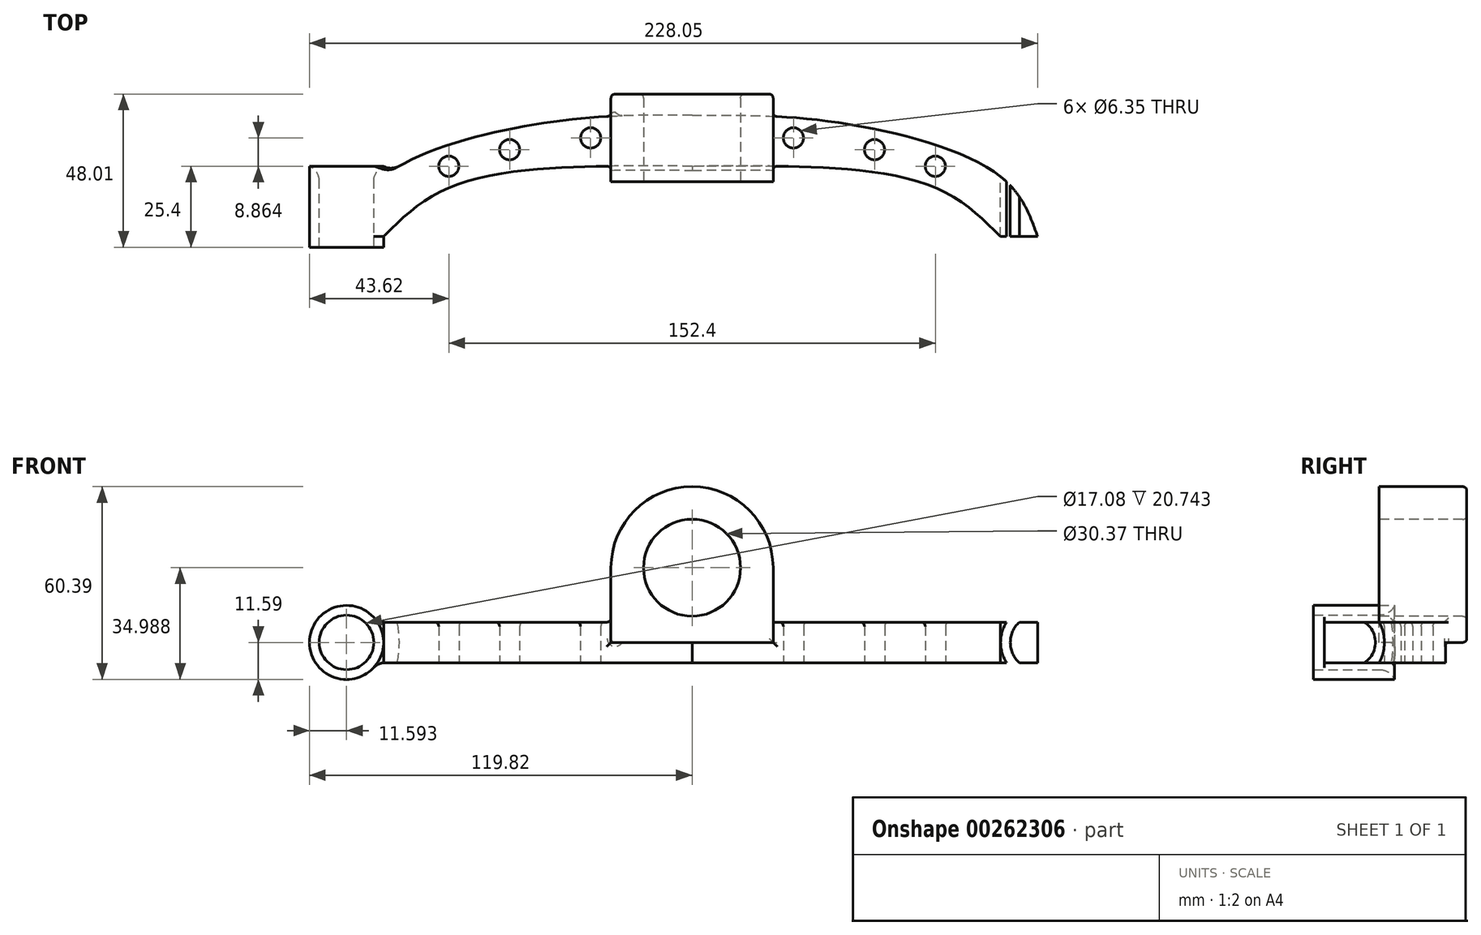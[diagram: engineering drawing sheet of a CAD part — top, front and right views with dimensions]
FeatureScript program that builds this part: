
annotation { "Feature Type Name" : "Feature", "Feature Type Description" : "" }
export const myFeature = defineFeature(function(context is Context, id is Id, definition is map)
    precondition{}
    {
        {
            var Q0;
            Q0=qCreatedBy(makeId("Top.planeOp"),FACE);
            var sketch = newSketch(context, id + "F0", { "sketchPlane" : qUnion([Q0])});
            skFitSpline(sketch, "E0", {"points": [v(0, 15.99) * mm, v(-43.29, 14) * mm, v(-96.35, -3.02) * mm, v(-108.23, -22.03) * mm], "startDerivative": vector(-114.23, 0) * mm, "endDerivative": vector(-28.32, -80.2) * mm});
            skLineSegment(sketch, "E1", {"start": v(0, 49.85) * mm, "end": v(0, -44) * mm, "construction": true});
            skFitSpline(sketch, "E2.MirrorCS", {"points": [v(0, 15.99) * mm, v(43.29, 14) * mm, v(96.35, -3.02) * mm, v(108.23, -22.03) * mm], "startDerivative": vector(114.23, 0) * mm, "endDerivative": vector(28.32, -80.2) * mm});
            skFitSpline(sketch, "E3", {"points": [v(0, 0) * mm, v(-27.26, 0) * mm, v(-73.98, -5.82) * mm, v(-96.64, -22.03) * mm], "startDerivative": vector(-81.32, 0.87) * mm, "endDerivative": vector(-62.2, -62.12) * mm});
            skFitSpline(sketch, "E4.MirrorCS", {"points": [v(0, 0) * mm, v(27.26, 0) * mm, v(73.98, -5.82) * mm, v(96.64, -22.03) * mm], "startDerivative": vector(81.32, 0.87) * mm, "endDerivative": vector(62.2, -62.12) * mm});
            skLineSegment(sketch, "E5", {"start": v(-96.64, -22.03) * mm, "end": v(-108.23, -22.03) * mm});
            skLineSegment(sketch, "E6", {"start": v(96.64, -22.03) * mm, "end": v(108.23, -22.03) * mm});
            skCircle(sketch, "E7", {"center": v(-76.2, 0) * mm, "radius": 3.18 * mm});
            skCircle(sketch, "E8", {"center": v(-57.15, 5.18) * mm, "radius": 3.18 * mm});
            skCircle(sketch, "E9", {"center": v(-31.75, 8.86) * mm, "radius": 3.18 * mm});
            skFitSpline(sketch, "E10.0", {"points": [v(0, 9.64) * mm, v(-2.4, 9.64) * mm, v(-7.16, 9.65) * mm, v(-14.32, 9.63) * mm, v(-21.64, 9.48) * mm, v(-27.97, 9.16) * mm, v(-33.23, 8.75) * mm, v(-37.3, 8.35) * mm, v(-41.49, 7.86) * mm, v(-45.84, 7.24) * mm, v(-50.31, 6.51) * mm, v(-56.36, 5.39) * mm, v(-63.97, 3.7) * mm, v(-71.31, 1.65) * mm, v(-76.8, -0.18) * mm, v(-80.7, -1.65) * mm, v(-84.28, -3.2) * mm, v(-86.97, -4.55) * mm, v(-88.92, -5.65) * mm, v(-90.27, -6.48) * mm, v(-91.3, -7.18) * mm, v(-92.06, -7.73) * mm, v(-92.77, -8.28) * mm, v(-93.6, -8.97) * mm, v(-94.8, -10.09) * mm, v(-96.1, -11.52) * mm, v(-97.43, -13.3) * mm, v(-98.57, -15.2) * mm, v(-99.58, -17.21) * mm, v(-100.8, -20.1) * mm, v(-101.65, -22.47) * mm, v(-102.24, -24.14) * mm], "construction": true});
            skCircle(sketch, "E11.MirrorC", {"center": v(31.75, 8.86) * mm, "radius": 3.18 * mm});
            skCircle(sketch, "E12.MirrorC", {"center": v(57.15, 5.18) * mm, "radius": 3.18 * mm});
            skCircle(sketch, "E13.MirrorC", {"center": v(76.2, 0) * mm, "radius": 3.18 * mm});
            skSolve(sketch);
        }
        {
            var Q0;
            Q0=makeQuery(id+"F0.imprint","IMPRINT",FACE,{"disambiguationData":[TD([[makeQuery(id+"F0.imprint","IMPRINT",EDGE,{"derivedFrom":sQuery(id+"F0.wireOp",EDGE,"E0")}),1.0]])]});
            extrude(context, id + "F1", {"entities" : qUnion([Q0]), "endBound" : BoundingType.SYMMETRIC, "depth" : 12.7 * mm});
        }
        {
            var Q0;
            Q0=makeQuery(id+"F1.opExtrude","CAP_EDGE",EDGE,{"disambiguationData":[OSD([sQuery(id+"F0.wireOp",EDGE,"E7")])],"isStart":false});
            var Q1;
            Q1=makeQuery(id+"F1.opExtrude","CAP_EDGE",EDGE,{"disambiguationData":[OSD([sQuery(id+"F0.wireOp",EDGE,"E8")])],"isStart":false});
            var Q2;
            Q2=makeQuery(id+"F1.opExtrude","CAP_EDGE",EDGE,{"disambiguationData":[OSD([sQuery(id+"F0.wireOp",EDGE,"E9")])],"isStart":false});
            var Q3;
            Q3=makeQuery(id+"F1.opExtrude","CAP_EDGE",EDGE,{"disambiguationData":[OSD([sQuery(id+"F0.wireOp",EDGE,"E11.MirrorC")])],"isStart":false});
            var Q4;
            Q4=makeQuery(id+"F1.opExtrude","CAP_EDGE",EDGE,{"disambiguationData":[OSD([sQuery(id+"F0.wireOp",EDGE,"E12.MirrorC")])],"isStart":false});
            var Q5;
            Q5=makeQuery(id+"F1.opExtrude","CAP_EDGE",EDGE,{"disambiguationData":[OSD([sQuery(id+"F0.wireOp",EDGE,"E13.MirrorC")])],"isStart":false});
            fillet(context, id + "F2", {"entities" : qUnion([Q0, Q1, Q2, Q3, Q4, Q5]), "radius" : 1.27 * mm, "tangentPropagation" : true, "allowEdgeOverflow" : false});
        }
        {
            var Q0;
            Q0=qCreatedBy(makeId("Front.planeOp"),FACE);
            var sketch = newSketch(context, id + "F3", { "sketchPlane" : qUnion([Q0])});
            skPoint(sketch, "E14.0", {"position": v(-96.64, 0) * mm});
            skPoint(sketch, "E15.0", {"position": v(-108.23, 0) * mm});
            skCircle(sketch, "E16", {"center": v(-108.23, 0) * mm, "radius": 11.6 * mm});
            skCircle(sketch, "E17", {"center": v(-108.23, 0) * mm, "radius": 8.54 * mm});
            skLineSegment(sketch, "E18", {"start": v(0, 0) * mm, "end": v(0, 47.64) * mm, "construction": true});
            skCircle(sketch, "E19.MirrorC", {"center": v(108.23, 0) * mm, "radius": 11.6 * mm});
            skCircle(sketch, "E20.MirrorC", {"center": v(108.23, 0) * mm, "radius": 8.54 * mm});
            skSolve(sketch);
        }
        {
            var Q0;
            Q0=makeQuery(id+"F3.imprint","IMPRINT",FACE,{"disambiguationData":[TD([[makeQuery(id+"F3.imprint","IMPRINT",EDGE,{"derivedFrom":sQuery(id+"F3.wireOp",EDGE,"E16")}),1.0]])]});
            var Q1;
            Q1=makeQuery(id+"F3.imprint","IMPRINT",FACE,{"disambiguationData":[TD([[makeQuery(id+"F3.imprint","IMPRINT",EDGE,{"derivedFrom":sQuery(id+"F3.wireOp",EDGE,"E19.MirrorC")}),-1.0]])]});
            extrude(context, id + "F4", {"entities" : qUnion([Q0, Q1]), "operationType" : NewBodyOperationType.ADD, "depth" : 25.4 * mm});
        }
        {
            var Q0;
            Q0=makeQuery(id+"F3.imprint","IMPRINT",FACE,{"disambiguationData":[TD([[makeQuery(id+"F3.imprint","IMPRINT",EDGE,{"derivedFrom":sQuery(id+"F3.wireOp",EDGE,"E17")}),1.0]])]});
            var Q1;
            Q1=makeQuery(id+"F3.imprint","IMPRINT",FACE,{"disambiguationData":[TD([[makeQuery(id+"F3.imprint","IMPRINT",EDGE,{"derivedFrom":sQuery(id+"F3.wireOp",EDGE,"E20.MirrorC")}),-1.0]])]});
            extrude(context, id + "F5", {"entities" : qUnion([Q0, Q1]), "operationType" : NewBodyOperationType.REMOVE, "endBound" : BoundingType.THROUGH_ALL, "depth" : 25.4 * mm});
        }
        {
            var Q0;
            Q0=makeQuery(id+"F4.opExtrude","CAP_EDGE",EDGE,{"disambiguationData":[OSD([sQuery(id+"F3.wireOp",EDGE,"E17")])],"isStart":true});
            var Q1;
            Q1=makeQuery(id+"F4.boolean.opBoolean","INTERSECT",EDGE,{"derivedFrom":[makeQuery(id+"F1.opExtrude","CAP_FACE",FACE,{"disambiguationData":[OSD([sQuery(id+"F0.wireOp",EDGE,"E0"),sQuery(id+"F0.wireOp",EDGE,"E2.MirrorCS"),sQuery(id+"F0.wireOp",EDGE,"E3"),sQuery(id+"F0.wireOp",EDGE,"E4.MirrorCS"),sQuery(id+"F0.wireOp",EDGE,"E5"),sQuery(id+"F0.wireOp",EDGE,"E6"),sQuery(id+"F0.wireOp",EDGE,"E7"),sQuery(id+"F0.wireOp",EDGE,"E8"),sQuery(id+"F0.wireOp",EDGE,"E9"),sQuery(id+"F0.wireOp",EDGE,"E11.MirrorC"),sQuery(id+"F0.wireOp",EDGE,"E12.MirrorC"),sQuery(id+"F0.wireOp",EDGE,"E13.MirrorC")])],"isStart":false}),makeQuery(id+"F4.opExtrude","SWEPT_FACE",FACE,{"disambiguationData":[OSD([sQuery(id+"F3.wireOp",EDGE,"E16")])]})]});
            var Q2;
            Q2=makeQuery(id+"F4.boolean.opBoolean","INTERSECT",EDGE,{"derivedFrom":[makeQuery(id+"F1.opExtrude","SWEPT_FACE",FACE,{"disambiguationData":[OSD([sQuery(id+"F0.wireOp",EDGE,"E0")])]}),makeQuery(id+"F4.opExtrude","SWEPT_FACE",FACE,{"disambiguationData":[OSD([sQuery(id+"F3.wireOp",EDGE,"E16")])]})]});
            var Q3;
            Q3=makeQuery(id+"F4.boolean.opBoolean","INTERSECT",EDGE,{"derivedFrom":[makeQuery(id+"F1.opExtrude","CAP_FACE",FACE,{"disambiguationData":[OSD([sQuery(id+"F0.wireOp",EDGE,"E0"),sQuery(id+"F0.wireOp",EDGE,"E2.MirrorCS"),sQuery(id+"F0.wireOp",EDGE,"E3"),sQuery(id+"F0.wireOp",EDGE,"E4.MirrorCS"),sQuery(id+"F0.wireOp",EDGE,"E5"),sQuery(id+"F0.wireOp",EDGE,"E6"),sQuery(id+"F0.wireOp",EDGE,"E7"),sQuery(id+"F0.wireOp",EDGE,"E8"),sQuery(id+"F0.wireOp",EDGE,"E9"),sQuery(id+"F0.wireOp",EDGE,"E11.MirrorC"),sQuery(id+"F0.wireOp",EDGE,"E12.MirrorC"),sQuery(id+"F0.wireOp",EDGE,"E13.MirrorC")])],"isStart":true}),makeQuery(id+"F4.opExtrude","SWEPT_FACE",FACE,{"disambiguationData":[OSD([sQuery(id+"F3.wireOp",EDGE,"E16")])]})]});
            var Q4;
            Q4=makeQuery(id+"F4.opExtrude","CAP_EDGE",EDGE,{"disambiguationData":[OSD([sQuery(id+"F3.wireOp",EDGE,"E20.MirrorC")])],"isStart":true});
            var Q5;
            Q5=makeQuery(id+"F4.boolean.opBoolean","INTERSECT",EDGE,{"derivedFrom":[makeQuery(id+"F1.opExtrude","CAP_FACE",FACE,{"disambiguationData":[OSD([sQuery(id+"F0.wireOp",EDGE,"E0"),sQuery(id+"F0.wireOp",EDGE,"E2.MirrorCS"),sQuery(id+"F0.wireOp",EDGE,"E3"),sQuery(id+"F0.wireOp",EDGE,"E4.MirrorCS"),sQuery(id+"F0.wireOp",EDGE,"E5"),sQuery(id+"F0.wireOp",EDGE,"E6"),sQuery(id+"F0.wireOp",EDGE,"E7"),sQuery(id+"F0.wireOp",EDGE,"E8"),sQuery(id+"F0.wireOp",EDGE,"E9"),sQuery(id+"F0.wireOp",EDGE,"E11.MirrorC"),sQuery(id+"F0.wireOp",EDGE,"E12.MirrorC"),sQuery(id+"F0.wireOp",EDGE,"E13.MirrorC")])],"isStart":false}),makeQuery(id+"F4.opExtrude","SWEPT_FACE",FACE,{"disambiguationData":[OSD([sQuery(id+"F3.wireOp",EDGE,"E19.MirrorC")])]})]});
            var Q6;
            Q6=makeQuery(id+"F4.boolean.opBoolean","INTERSECT",EDGE,{"derivedFrom":[makeQuery(id+"F1.opExtrude","SWEPT_FACE",FACE,{"disambiguationData":[OSD([sQuery(id+"F0.wireOp",EDGE,"E2.MirrorCS")])]}),makeQuery(id+"F4.opExtrude","SWEPT_FACE",FACE,{"disambiguationData":[OSD([sQuery(id+"F3.wireOp",EDGE,"E19.MirrorC")])]})]});
            var Q7;
            Q7=makeQuery(id+"F4.boolean.opBoolean","INTERSECT",EDGE,{"derivedFrom":[makeQuery(id+"F1.opExtrude","CAP_FACE",FACE,{"disambiguationData":[OSD([sQuery(id+"F0.wireOp",EDGE,"E0"),sQuery(id+"F0.wireOp",EDGE,"E2.MirrorCS"),sQuery(id+"F0.wireOp",EDGE,"E3"),sQuery(id+"F0.wireOp",EDGE,"E4.MirrorCS"),sQuery(id+"F0.wireOp",EDGE,"E5"),sQuery(id+"F0.wireOp",EDGE,"E6"),sQuery(id+"F0.wireOp",EDGE,"E7"),sQuery(id+"F0.wireOp",EDGE,"E8"),sQuery(id+"F0.wireOp",EDGE,"E9"),sQuery(id+"F0.wireOp",EDGE,"E11.MirrorC"),sQuery(id+"F0.wireOp",EDGE,"E12.MirrorC"),sQuery(id+"F0.wireOp",EDGE,"E13.MirrorC")])],"isStart":true}),makeQuery(id+"F4.opExtrude","SWEPT_FACE",FACE,{"disambiguationData":[OSD([sQuery(id+"F3.wireOp",EDGE,"E19.MirrorC")])]})]});
            fillet(context, id + "F6", {"entities" : qUnion([Q0, Q1, Q2, Q3, Q4, Q5, Q6, Q7]), "radius" : 5.08 * mm, "tangentPropagation" : true, "allowEdgeOverflow" : false});
        }
        {
            var Q0;
            Q0=qCreatedBy(makeId("Front.planeOp"),FACE);
            var sketch = newSketch(context, id + "F7", { "sketchPlane" : qUnion([Q0])});
            skLineSegment(sketch, "E21", {"start": v(0, -20.34) * mm, "end": v(0, 23.4) * mm, "construction": true});
            skLineSegment(sketch, "E22.0", {"start": v(25.4, 0) * mm, "end": v(25.4, 23.4) * mm});
            skLineSegment(sketch, "E23.MirrorCS", {"start": v(-25.4, 0) * mm, "end": v(-25.4, 23.4) * mm});
            skFitSpline(sketch, "E24.0", {"points": [v(0, 0) * mm, v(-8.15, 0) * mm, v(-27, 0) * mm, v(-75.77, 0) * mm, v(-90.33, 0) * mm, v(-96.64, 0) * mm]});
            skFitSpline(sketch, "E25.0", {"points": [v(0, 0) * mm, v(8.15, 0) * mm, v(27, 0) * mm, v(75.77, 0) * mm, v(90.33, 0) * mm, v(96.64, 0) * mm]});
            skPoint(sketch, "E26.orphan", {"position": v(-25.4, -20.34) * mm});
            skPoint(sketch, "E27.orphan", {"position": v(25.4, -20.34) * mm});
            skArc(sketch, "E28", {"start": v(25.4, 23.4) * mm, "mid": v(0, 48.8) * mm, "end": v(-25.4, 23.4) * mm});
            skCircle(sketch, "E29", {"center": v(0, 23.4) * mm, "radius": 15.19 * mm});
            skSolve(sketch);
        }
        {
            var Q0;
            {var subQ1=sQuery(id+"F7.wireOp",EDGE,"E22.0");Q0=makeQuery(id+"F7.imprint","IMPRINT",FACE,{"disambiguationData":[TD([[makeQuery(id+"F7.imprint","IMPRINT",EDGE,{"derivedFrom":subQ1}),1.0]])]});}
            extrude(context, id + "F8", {"entities" : qUnion([Q0]), "operationType" : NewBodyOperationType.ADD, "oppositeDirection" : true, "depth" : 22.6 * mm, "hasSecondDirection" : true, "secondDirectionOppositeDirection" : false, "secondDirectionDepth" : 4.83 * mm});
        }
        {
            var Q0;
            {var subQ0=sQuery(id+"F0.wireOp",EDGE,"E0");var subQ11=sQuery(id+"F0.wireOp",EDGE,"E2.MirrorCS");Q0=makeQuery(id+"F8.boolean.opBoolean","INTERSECT",EDGE,{"derivedFrom":[makeQuery(id+"F4.boolean.opBoolean","SPLIT",FACE,{"disambiguationData":[TD([makeQuery(id+"F1.opExtrude","SWEPT_FACE",FACE,{"disambiguationData":[OSD([subQ0])]})])],"derivedFrom":makeQuery(id+"F1.opExtrude","SWEPT_FACE",FACE,{"disambiguationData":[OSD([subQ11])]})}),makeQuery(id+"F8.opExtrude","SWEPT_FACE",FACE,{"disambiguationData":[OSD([sQuery(id+"F7.wireOp",EDGE,"E22.0")])]})]});}
            var Q1;
            Q1=makeQuery(id+"F8.opExtrude","CAP_EDGE",EDGE,{"disambiguationData":[OSD([sQuery(id+"F7.wireOp",EDGE,"E29")])],"isStart":false});
            var Q2;
            Q2=makeQuery(id+"F8.opExtrude","CAP_EDGE",EDGE,{"disambiguationData":[OSD([sQuery(id+"F7.wireOp",EDGE,"E25.0")])],"isStart":false});
            var Q3;
            Q3=makeQuery(id+"F8.opExtrude","CAP_EDGE",EDGE,{"disambiguationData":[OSD([sQuery(id+"F7.wireOp",EDGE,"E24.0")])],"isStart":false});
            var Q4;
            {var subQ0=sQuery(id+"F7.wireOp",EDGE,"E23.MirrorCS");var subQ1=sQuery(id+"F7.wireOp",EDGE,"E24.0");Q4=makeQuery(id+"F8.boolean.opBoolean","SPLIT",EDGE,{"disambiguationData":[TD([makeQuery(id+"F1.opExtrude","SWEPT_FACE",FACE,{"disambiguationData":[OSD([sQuery(id+"F0.wireOp",EDGE,"E0")])]})])],"derivedFrom":makeQuery(id+"F8.opExtrude","SWEPT_EDGE",EDGE,{"disambiguationData":[OSD([subQ0,subQ1])]})});}
            var Q5;
            {var subQ10=sQuery(id+"F0.wireOp",EDGE,"E2.MirrorCS");var subQ11=sQuery(id+"F0.wireOp",EDGE,"E0");Q5=makeQuery(id+"F8.boolean.opBoolean","INTERSECT",EDGE,{"derivedFrom":[makeQuery(id+"F4.boolean.opBoolean","SPLIT",FACE,{"disambiguationData":[TD([makeQuery(id+"F1.opExtrude","SWEPT_FACE",FACE,{"disambiguationData":[OSD([subQ10])]})])],"derivedFrom":makeQuery(id+"F1.opExtrude","SWEPT_FACE",FACE,{"disambiguationData":[OSD([subQ11])]})}),makeQuery(id+"F8.opExtrude","SWEPT_FACE",FACE,{"disambiguationData":[OSD([sQuery(id+"F7.wireOp",EDGE,"E23.MirrorCS")])]})]});}
            var Q6;
            {var subQ0=sQuery(id+"F0.wireOp",EDGE,"E7");var subQ1=sQuery(id+"F0.wireOp",EDGE,"E6");var subQ2=sQuery(id+"F0.wireOp",EDGE,"E5");var subQ3=sQuery(id+"F0.wireOp",EDGE,"E0");var subQ4=sQuery(id+"F0.wireOp",EDGE,"E8");var subQ5=sQuery(id+"F0.wireOp",EDGE,"E2.MirrorCS");var subQ6=sQuery(id+"F0.wireOp",EDGE,"E11.MirrorC");var subQ7=sQuery(id+"F0.wireOp",EDGE,"E3");var subQ8=sQuery(id+"F0.wireOp",EDGE,"E9");var subQ9=sQuery(id+"F0.wireOp",EDGE,"E4.MirrorCS");var subQ10=sQuery(id+"F0.wireOp",EDGE,"E12.MirrorC");var subQ11=sQuery(id+"F0.wireOp",EDGE,"E13.MirrorC");Q6=makeQuery(id+"F8.boolean.opBoolean","INTERSECT",EDGE,{"derivedFrom":[makeQuery(id+"F4.boolean.opBoolean","SPLIT",FACE,{"disambiguationData":[TD([makeQuery(id+"F1.opExtrude","SWEPT_FACE",FACE,{"disambiguationData":[OSD([subQ7])]})])],"derivedFrom":makeQuery(id+"F1.opExtrude","CAP_FACE",FACE,{"disambiguationData":[OSD([subQ3,subQ5,subQ7,subQ9,subQ2,subQ1,subQ0,subQ4,subQ8,subQ6,subQ10,subQ11])],"isStart":false})}),makeQuery(id+"F8.opExtrude","SWEPT_FACE",FACE,{"disambiguationData":[OSD([sQuery(id+"F7.wireOp",EDGE,"E23.MirrorCS")])]})]});}
            var Q7;
            Q7=makeQuery(id+"F8.boolean.opBoolean","INTERSECT",EDGE,{"derivedFrom":[makeQuery(id+"F1.opExtrude","SWEPT_FACE",FACE,{"disambiguationData":[OSD([sQuery(id+"F0.wireOp",EDGE,"E3")])]}),makeQuery(id+"F8.opExtrude","SWEPT_FACE",FACE,{"disambiguationData":[OSD([sQuery(id+"F7.wireOp",EDGE,"E24.0")])]})]});
            var Q8;
            Q8=makeQuery(id+"F8.boolean.opBoolean","INTERSECT",EDGE,{"derivedFrom":[makeQuery(id+"F1.opExtrude","SWEPT_FACE",FACE,{"disambiguationData":[OSD([sQuery(id+"F0.wireOp",EDGE,"E3")])]}),makeQuery(id+"F8.opExtrude","SWEPT_FACE",FACE,{"disambiguationData":[OSD([sQuery(id+"F7.wireOp",EDGE,"E23.MirrorCS")])]})]});
            var Q9;
            Q9=makeQuery(id+"F8.boolean.opBoolean","INTERSECT",EDGE,{"derivedFrom":[makeQuery(id+"F1.opExtrude","SWEPT_FACE",FACE,{"disambiguationData":[OSD([sQuery(id+"F0.wireOp",EDGE,"E4.MirrorCS")])]}),makeQuery(id+"F8.opExtrude","SWEPT_FACE",FACE,{"disambiguationData":[OSD([sQuery(id+"F7.wireOp",EDGE,"E22.0")])]})]});
            var Q10;
            Q10=makeQuery(id+"F8.boolean.opBoolean","INTERSECT",EDGE,{"derivedFrom":[makeQuery(id+"F1.opExtrude","SWEPT_FACE",FACE,{"disambiguationData":[OSD([sQuery(id+"F0.wireOp",EDGE,"E4.MirrorCS")])]}),makeQuery(id+"F8.opExtrude","SWEPT_FACE",FACE,{"disambiguationData":[OSD([sQuery(id+"F7.wireOp",EDGE,"E25.0")])]})]});
            var Q11;
            Q11=makeQuery(id+"F8.opExtrude","CAP_EDGE",EDGE,{"disambiguationData":[OSD([sQuery(id+"F7.wireOp",EDGE,"E23.MirrorCS")])],"isStart":false});
            var Q12;
            Q12=makeQuery(id+"F8.opExtrude","CAP_EDGE",EDGE,{"disambiguationData":[OSD([sQuery(id+"F7.wireOp",EDGE,"E28")])],"isStart":false});
            fillet(context, id + "F9", {"entities" : qUnion([Q0, Q1, Q2, Q3, Q4, Q5, Q6, Q7, Q8, Q9, Q10, Q11, Q12]), "radius" : 1.27 * mm, "tangentPropagation" : true, "allowEdgeOverflow" : false});
        }
    });
